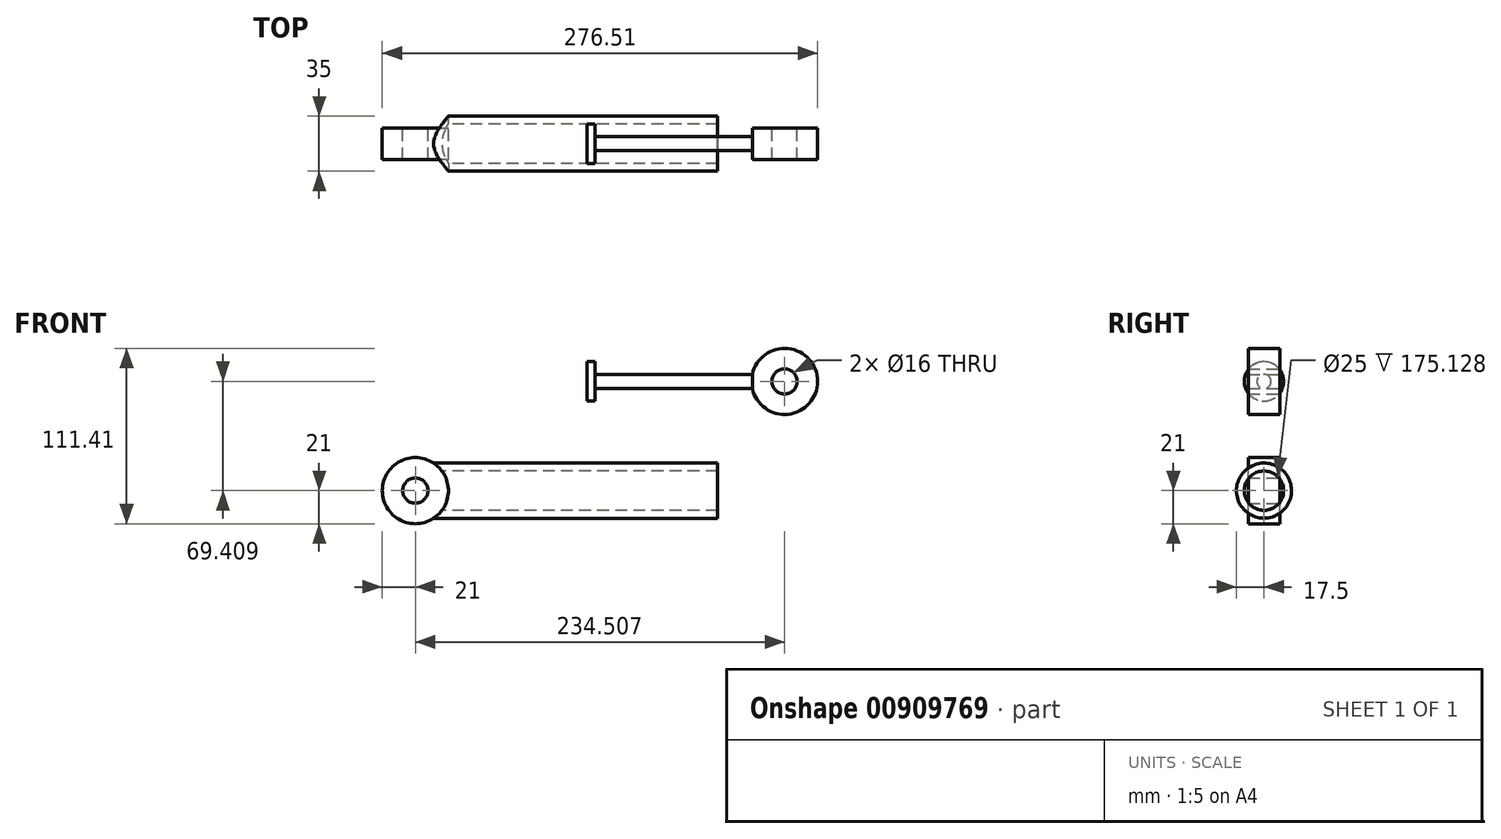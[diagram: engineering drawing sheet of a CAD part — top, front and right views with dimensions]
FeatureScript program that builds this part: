
annotation { "Feature Type Name" : "Feature", "Feature Type Description" : "" }
export const myFeature = defineFeature(function(context is Context, id is Id, definition is map)
    precondition{}
    {
        {
            var Q0;
            Q0=qCreatedBy(makeId("Right.planeOp"),FACE);
            var sketch = newSketch(context, id + "F0", { "sketchPlane" : qUnion([Q0])});
            skCircle(sketch, "E0", {"center": v(0, 0) * mm, "radius": 12.5 * mm});
            skCircle(sketch, "E1", {"center": v(0, 0) * mm, "radius": 17.5 * mm});
            skSolve(sketch);
        }
        {
            var Q0;
            Q0 = qSketchRegion(id + "F0", true);
            extrude(context, id + "F1", {"entities" : qUnion([Q0]), "endBound" : BoundingType.SYMMETRIC, "depth" : (56 + 100) * mm, "offsetDistance" : 25 * mm});
        }
        {
            var Q0;
            Q0=qCreatedBy(makeId("Front.planeOp"),FACE);
            var sketch = newSketch(context, id + "F2", { "sketchPlane" : qUnion([Q0])});
            skCircle(sketch, "E2", {"center": v(-114, 0) * mm, "radius": 8 * mm});
            skCircle(sketch, "E3", {"center": v(-114, 0) * mm, "radius": 21 * mm});
            skSolve(sketch);
        }
        {
            var Q0;
            Q0=makeQuery(id+"F2.imprint","IMPRINT",FACE,{"disambiguationData":[TD([[makeQuery(id+"F2.imprint","IMPRINT",EDGE,{"derivedFrom":sQuery(id+"F2.wireOp",EDGE,"E2")}),-1.0]])]});
            extrude(context, id + "F3", {"entities" : qUnion([Q0]), "operationType" : NewBodyOperationType.ADD, "endBound" : BoundingType.SYMMETRIC, "depth" : 40 * mm, "offsetDistance" : 25 * mm});
        }
        {
            var Q0;
            Q0=makeQuery(id+"F1.opExtrude","CAP_FACE",FACE,{"disambiguationData":[OSD([sQuery(id+"F0.wireOp",EDGE,"E0"),sQuery(id+"F0.wireOp",EDGE,"E1")])],"isStart":true});
            var Q1;
            Q1=makeQuery(id+"F3.opExtrude","SWEPT_BODY",BODY,{"disambiguationData":[OSD([sQuery(id+"F2.wireOp",EDGE,"E2"),sQuery(id+"F2.wireOp",EDGE,"E3")])]});
            extrude(context, id + "F4", {"entities" : qUnion([Q0]), "operationType" : NewBodyOperationType.ADD, "endBound" : BoundingType.UP_TO_BODY, "depth" : 25 * mm, "endBoundEntityBody" : qUnion([Q1]), "offsetDistance" : 25 * mm});
        }
        {
            var Q0;
            Q0=qCreatedBy(makeId("Right.planeOp"),FACE);
            var sketch = newSketch(context, id + "F5", { "sketchPlane" : qUnion([Q0])});
            skCircle(sketch, "E4", {"center": v(0, 69.4) * mm, "radius": 12.5 * mm});
            skCircle(sketch, "E5", {"center": v(0, 69.4) * mm, "radius": 4.52 * mm});
            skSolve(sketch);
        }
        {
            var Q0;
            Q0=makeQuery(id+"F5.imprint","IMPRINT",FACE,{"disambiguationData":[TD([[makeQuery(id+"F5.imprint","IMPRINT",EDGE,{"derivedFrom":sQuery(id+"F5.wireOp",EDGE,"E5")}),1.0]])]});
            extrude(context, id + "F6", {"entities" : qUnion([Q0]), "depth" : 100 * mm, "offsetDistance" : 25 * mm});
        }
        {
            var Q0;
            Q0 = qSketchRegion(id + "F5", true);
            var Q1;
            Q1=makeQuery(id+"F6.opExtrude","CAP_FACE",FACE,{"disambiguationData":[OSD([sQuery(id+"F5.wireOp",EDGE,"E5")])],"isStart":true});
            extrude(context, id + "F7", {"entities" : qUnion([Q0, Q1]), "operationType" : NewBodyOperationType.ADD, "oppositeDirection" : true, "depth" : 5 * mm, "offsetDistance" : 25 * mm});
        }
        {
            var Q0;
            Q0=qCreatedBy(makeId("Front.planeOp"),FACE);
            var sketch = newSketch(context, id + "F8", { "sketchPlane" : qUnion([Q0])});
            skCircle(sketch, "E6", {"center": v(120.5, 69.4) * mm, "radius": 8 * mm});
            skCircle(sketch, "E7", {"center": v(120.5, 69.4) * mm, "radius": 21 * mm});
            skLineSegment(sketch, "E8.0", {"start": v(100, 73.93) * mm, "end": v(100, 64.89) * mm});
            skSolve(sketch);
        }
        {
            var Q0;
            Q0=makeQuery(id+"F3.opExtrude","CAP_FACE",FACE,{"disambiguationData":[OSD([sQuery(id+"F2.wireOp",EDGE,"E2"),sQuery(id+"F2.wireOp",EDGE,"E3")])],"isStart":true});
            extrude(context, id + "F9", {"entities" : qUnion([Q0]), "operationType" : NewBodyOperationType.REMOVE, "oppositeDirection" : true, "depth" : 10 * mm, "offsetDistance" : 25 * mm});
        }
        {
            var Q0;
            Q0=makeQuery(id+"F3.opExtrude","CAP_FACE",FACE,{"disambiguationData":[OSD([sQuery(id+"F2.wireOp",EDGE,"E2"),sQuery(id+"F2.wireOp",EDGE,"E3")])],"isStart":false});
            extrude(context, id + "F10", {"entities" : qUnion([Q0]), "operationType" : NewBodyOperationType.REMOVE, "oppositeDirection" : true, "depth" : 10 * mm, "offsetDistance" : 25 * mm});
        }
        {
            var Q0;
            Q0=makeQuery(id+"F8.imprint","IMPRINT",FACE,{"disambiguationData":[TD([[makeQuery(id+"F8.imprint","IMPRINT",EDGE,{"derivedFrom":sQuery(id+"F8.wireOp",EDGE,"E6")}),-1.0]])]});
            extrude(context, id + "F11", {"entities" : qUnion([Q0]), "endBound" : BoundingType.SYMMETRIC, "depth" : 20 * mm, "offsetDistance" : 25 * mm});
        }
    });
